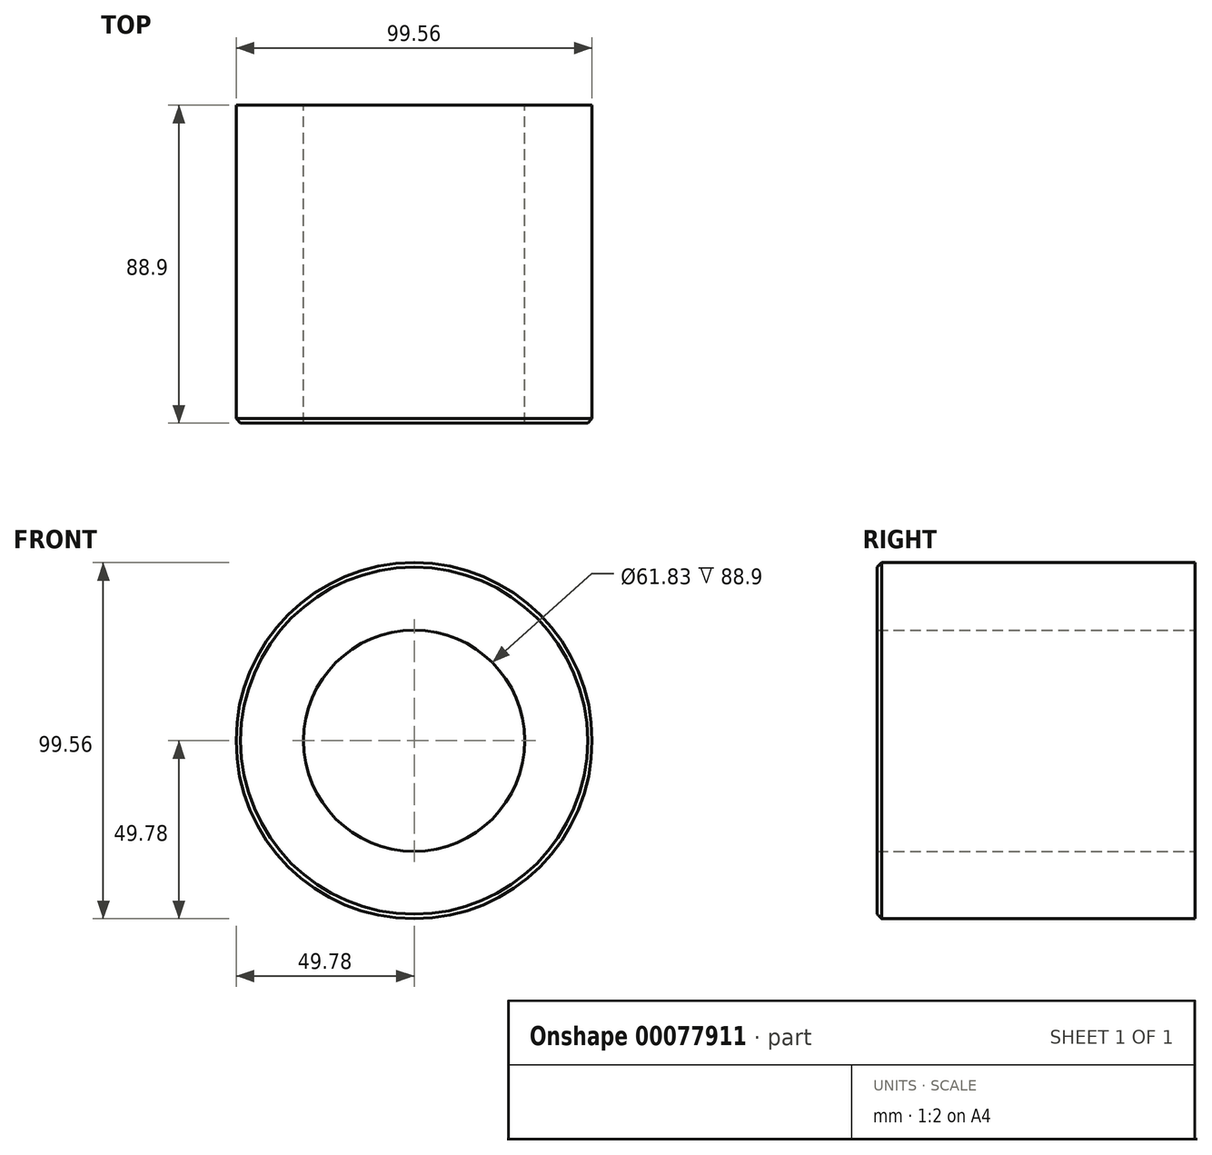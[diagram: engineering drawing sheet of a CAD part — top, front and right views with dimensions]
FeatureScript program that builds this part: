
annotation { "Feature Type Name" : "Feature", "Feature Type Description" : "" }
export const myFeature = defineFeature(function(context is Context, id is Id, definition is map)
    precondition{}
    {
        {
            var Q0;
            Q0=qCreatedBy(makeId("Front.planeOp"),FACE);
            var sketch = newSketch(context, id + "F0", { "sketchPlane" : qUnion([Q0])});
            skCircle(sketch, "E0", {"center": v(0, 0) * mm, "radius": 49.78 * mm});
            skCircle(sketch, "E1", {"center": v(0, 0) * mm, "radius": 30.92 * mm});
            skSolve(sketch);
        }
        {
            var Q0;
            Q0 = qSketchRegion(id + "F0", true);
            extrude(context, id + "F1", {"entities" : qUnion([Q0]), "depth" : 88.9 * mm});
        }
        {
            var Q0;
            Q0=makeQuery(id+"F1.opExtrude","CAP_EDGE",EDGE,{"disambiguationData":[OSD([sQuery(id+"F0.wireOp",EDGE,"E0")])],"isStart":false});
            chamfer(context, id + "F2", {"entities" : qUnion([Q0]), "width" : 1.27 * mm, "tangentPropagation" : true});
        }
    });
